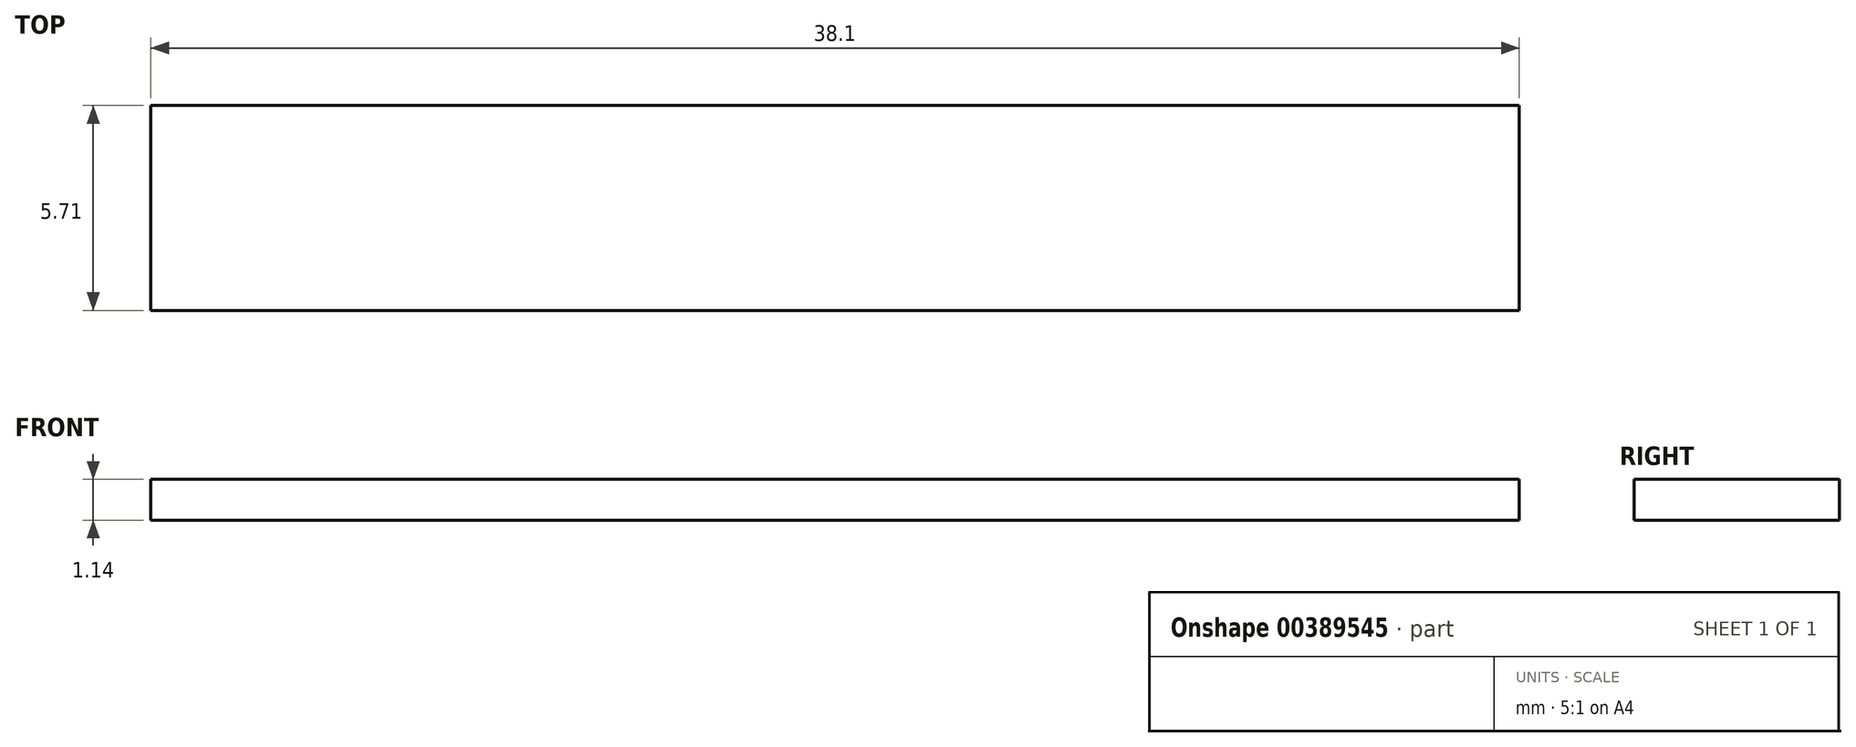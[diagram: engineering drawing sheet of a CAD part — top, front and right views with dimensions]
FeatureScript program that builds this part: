
annotation { "Feature Type Name" : "Feature", "Feature Type Description" : "" }
export const myFeature = defineFeature(function(context is Context, id is Id, definition is map)
    precondition{}
    {
        {
            var Q0;
            Q0=qCreatedBy(makeId("Top.planeOp"),FACE);
            var sketch = newSketch(context, id + "F0", { "sketchPlane" : qUnion([Q0])});
            skLineSegment(sketch, "E0", {"start": v(-3.59, 13.9) * mm, "end": v(-3.59, 8.19) * mm});
            skLineSegment(sketch, "E1", {"start": v(-3.59, 8.19) * mm, "end": v(34.51, 8.19) * mm});
            skLineSegment(sketch, "E2", {"start": v(34.51, 8.19) * mm, "end": v(34.51, 13.9) * mm});
            skLineSegment(sketch, "E3", {"start": v(34.51, 13.9) * mm, "end": v(-3.59, 13.9) * mm});
            skSolve(sketch);
        }
        {
            var Q0;
            Q0=makeQuery(id+"F0.imprint","IMPRINT",FACE,{"disambiguationData":[TD([[makeQuery(id+"F0.imprint","IMPRINT",EDGE,{"derivedFrom":sQuery(id+"F0.wireOp",EDGE,"E0")}),1.0]])]});
            extrude(context, id + "F1", {"entities" : qUnion([Q0]), "depth" : 1.14 * mm});
        }
    });
